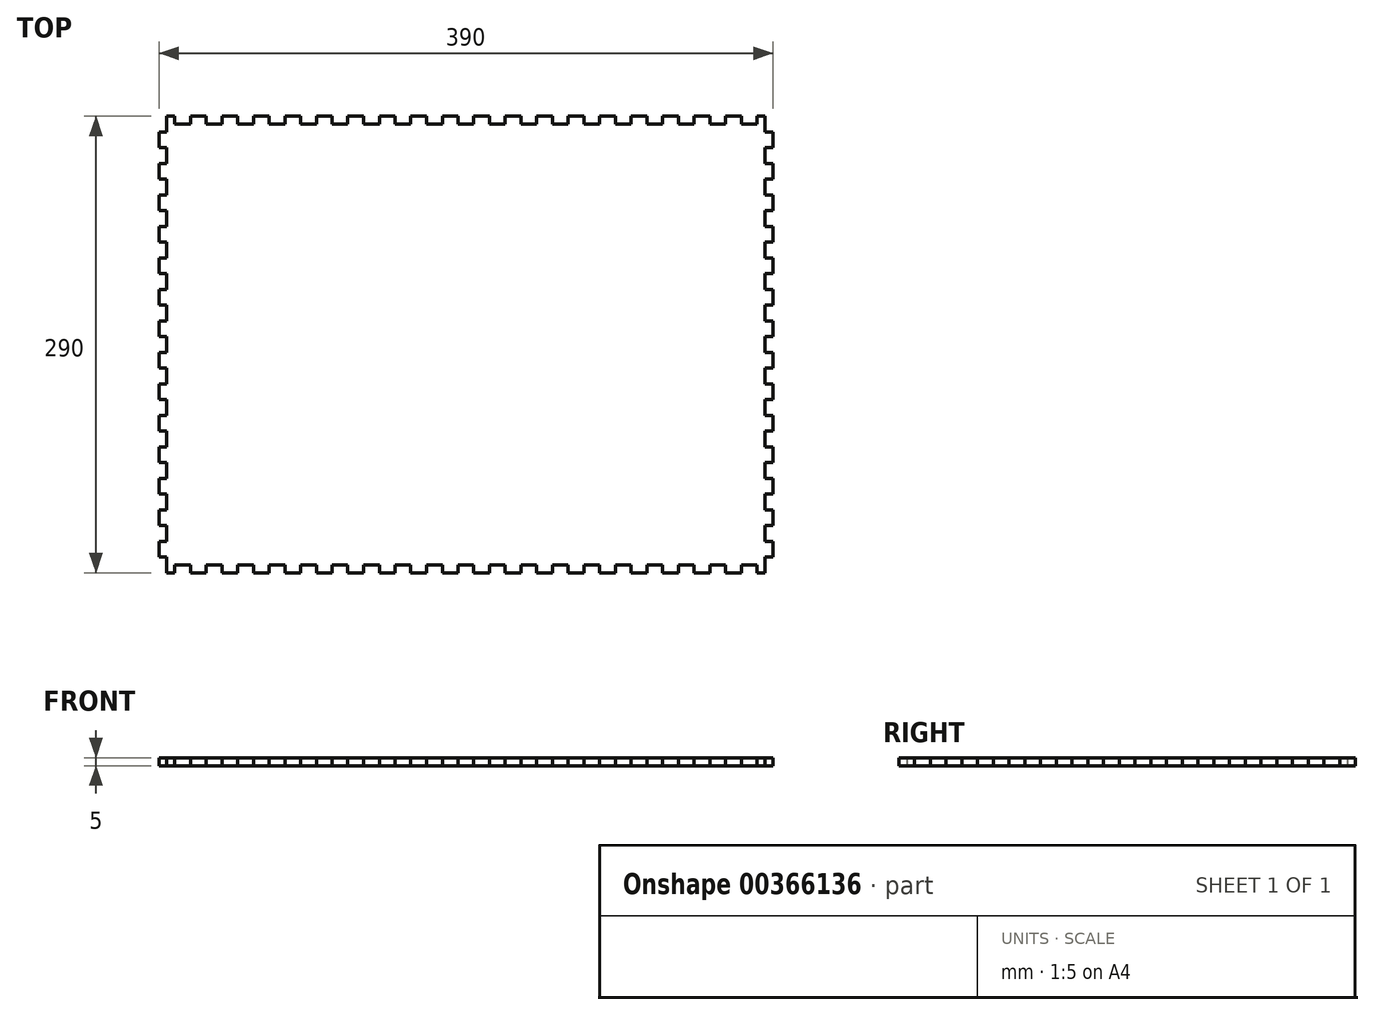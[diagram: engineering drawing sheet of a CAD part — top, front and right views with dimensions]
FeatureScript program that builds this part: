
annotation { "Feature Type Name" : "Feature", "Feature Type Description" : "" }
export const myFeature = defineFeature(function(context is Context, id is Id, definition is map)
    precondition{}
    {
        {
            var Q0;
            Q0=qCreatedBy(makeId("Top.planeOp"),FACE);
            var sketch = newSketch(context, id + "F0", { "sketchPlane" : qUnion([Q0])});
            skLineSegment(sketch, "E0", {"start": v(-189.05, -126.62) * mm, "end": v(-184.05, -126.62) * mm});
            skLineSegment(sketch, "E1", {"start": v(-184.05, -126.62) * mm, "end": v(-184.05, -136.62) * mm});
            skLineSegment(sketch, "E2", {"start": v(-184.05, -136.62) * mm, "end": v(-179.05, -136.62) * mm});
            skLineSegment(sketch, "E3", {"start": v(-179.05, -136.62) * mm, "end": v(-179.05, -131.62) * mm});
            skLineSegment(sketch, "E4", {"start": v(-179.05, -131.62) * mm, "end": v(-169.05, -131.62) * mm});
            skLineSegment(sketch, "E5", {"start": v(-169.05, -131.62) * mm, "end": v(-169.05, -136.62) * mm});
            skLineSegment(sketch, "E6", {"start": v(-169.05, -136.62) * mm, "end": v(-159.05, -136.62) * mm});
            skLineSegment(sketch, "E7", {"start": v(-159.05, -136.62) * mm, "end": v(-159.05, -131.62) * mm});
            skLineSegment(sketch, "E8", {"start": v(-159.05, -131.62) * mm, "end": v(-149.05, -131.62) * mm});
            skLineSegment(sketch, "E9", {"start": v(-149.05, -131.62) * mm, "end": v(-149.05, -136.62) * mm});
            skLineSegment(sketch, "E10.1.0.0", {"start": v(-149.05, -136.62) * mm, "end": v(-139.05, -136.62) * mm});
            skLineSegment(sketch, "E10.1.0.1", {"start": v(-139.05, -136.62) * mm, "end": v(-139.05, -131.62) * mm});
            skLineSegment(sketch, "E10.1.0.2", {"start": v(-139.05, -131.62) * mm, "end": v(-129.05, -131.62) * mm});
            skLineSegment(sketch, "E10.1.0.3", {"start": v(-129.05, -131.62) * mm, "end": v(-129.05, -136.62) * mm});
            skLineSegment(sketch, "E10.2.0.0", {"start": v(-129.05, -136.62) * mm, "end": v(-119.05, -136.62) * mm});
            skLineSegment(sketch, "E10.2.0.1", {"start": v(-119.05, -136.62) * mm, "end": v(-119.05, -131.62) * mm});
            skLineSegment(sketch, "E10.2.0.2", {"start": v(-119.05, -131.62) * mm, "end": v(-109.05, -131.62) * mm});
            skLineSegment(sketch, "E10.2.0.3", {"start": v(-109.05, -131.62) * mm, "end": v(-109.05, -136.62) * mm});
            skLineSegment(sketch, "E10.3.0.0", {"start": v(-109.05, -136.62) * mm, "end": v(-99.05, -136.62) * mm});
            skLineSegment(sketch, "E10.3.0.1", {"start": v(-99.05, -136.62) * mm, "end": v(-99.05, -131.62) * mm});
            skLineSegment(sketch, "E10.3.0.2", {"start": v(-99.05, -131.62) * mm, "end": v(-89.05, -131.62) * mm});
            skLineSegment(sketch, "E10.3.0.3", {"start": v(-89.05, -131.62) * mm, "end": v(-89.05, -136.62) * mm});
            skLineSegment(sketch, "E10.4.0.0", {"start": v(-89.05, -136.62) * mm, "end": v(-79.05, -136.62) * mm});
            skLineSegment(sketch, "E10.4.0.1", {"start": v(-79.05, -136.62) * mm, "end": v(-79.05, -131.62) * mm});
            skLineSegment(sketch, "E10.4.0.2", {"start": v(-79.05, -131.62) * mm, "end": v(-69.05, -131.62) * mm});
            skLineSegment(sketch, "E10.4.0.3", {"start": v(-69.05, -131.62) * mm, "end": v(-69.05, -136.62) * mm});
            skLineSegment(sketch, "E10.5.0.0", {"start": v(-69.05, -136.62) * mm, "end": v(-59.05, -136.62) * mm});
            skLineSegment(sketch, "E10.5.0.1", {"start": v(-59.05, -136.62) * mm, "end": v(-59.05, -131.62) * mm});
            skLineSegment(sketch, "E10.5.0.2", {"start": v(-59.05, -131.62) * mm, "end": v(-49.05, -131.62) * mm});
            skLineSegment(sketch, "E10.5.0.3", {"start": v(-49.05, -131.62) * mm, "end": v(-49.05, -136.62) * mm});
            skLineSegment(sketch, "E10.6.0.0", {"start": v(-49.05, -136.62) * mm, "end": v(-39.05, -136.62) * mm});
            skLineSegment(sketch, "E10.6.0.1", {"start": v(-39.05, -136.62) * mm, "end": v(-39.05, -131.62) * mm});
            skLineSegment(sketch, "E10.6.0.2", {"start": v(-39.05, -131.62) * mm, "end": v(-29.05, -131.62) * mm});
            skLineSegment(sketch, "E10.6.0.3", {"start": v(-29.05, -131.62) * mm, "end": v(-29.05, -136.62) * mm});
            skLineSegment(sketch, "E10.7.0.0", {"start": v(-29.05, -136.62) * mm, "end": v(-19.05, -136.62) * mm});
            skLineSegment(sketch, "E10.7.0.1", {"start": v(-19.05, -136.62) * mm, "end": v(-19.05, -131.62) * mm});
            skLineSegment(sketch, "E10.7.0.2", {"start": v(-19.05, -131.62) * mm, "end": v(-9.05, -131.62) * mm});
            skLineSegment(sketch, "E10.7.0.3", {"start": v(-9.05, -131.62) * mm, "end": v(-9.05, -136.62) * mm});
            skLineSegment(sketch, "E10.8.0.0", {"start": v(-9.05, -136.62) * mm, "end": v(0.95, -136.62) * mm});
            skLineSegment(sketch, "E10.8.0.1", {"start": v(0.95, -136.62) * mm, "end": v(0.95, -131.62) * mm});
            skLineSegment(sketch, "E10.8.0.2", {"start": v(0.95, -131.62) * mm, "end": v(10.95, -131.62) * mm});
            skLineSegment(sketch, "E10.8.0.3", {"start": v(10.95, -131.62) * mm, "end": v(10.95, -136.62) * mm});
            skLineSegment(sketch, "E10.9.0.0", {"start": v(10.95, -136.62) * mm, "end": v(20.95, -136.62) * mm});
            skLineSegment(sketch, "E10.9.0.1", {"start": v(20.95, -136.62) * mm, "end": v(20.95, -131.62) * mm});
            skLineSegment(sketch, "E10.9.0.2", {"start": v(20.95, -131.62) * mm, "end": v(30.95, -131.62) * mm});
            skLineSegment(sketch, "E10.9.0.3", {"start": v(30.95, -131.62) * mm, "end": v(30.95, -136.62) * mm});
            skLineSegment(sketch, "E10.10.0.0", {"start": v(30.95, -136.62) * mm, "end": v(40.95, -136.62) * mm});
            skLineSegment(sketch, "E10.10.0.1", {"start": v(40.95, -136.62) * mm, "end": v(40.95, -131.62) * mm});
            skLineSegment(sketch, "E10.10.0.2", {"start": v(40.95, -131.62) * mm, "end": v(50.95, -131.62) * mm});
            skLineSegment(sketch, "E10.10.0.3", {"start": v(50.95, -131.62) * mm, "end": v(50.95, -136.62) * mm});
            skLineSegment(sketch, "E10.11.0.0", {"start": v(50.95, -136.62) * mm, "end": v(60.95, -136.62) * mm});
            skLineSegment(sketch, "E10.11.0.1", {"start": v(60.95, -136.62) * mm, "end": v(60.95, -131.62) * mm});
            skLineSegment(sketch, "E10.11.0.2", {"start": v(60.95, -131.62) * mm, "end": v(70.95, -131.62) * mm});
            skLineSegment(sketch, "E10.11.0.3", {"start": v(70.95, -131.62) * mm, "end": v(70.95, -136.62) * mm});
            skLineSegment(sketch, "E10.12.0.0", {"start": v(70.95, -136.62) * mm, "end": v(80.95, -136.62) * mm});
            skLineSegment(sketch, "E10.12.0.1", {"start": v(80.95, -136.62) * mm, "end": v(80.95, -131.62) * mm});
            skLineSegment(sketch, "E10.12.0.2", {"start": v(80.95, -131.62) * mm, "end": v(90.95, -131.62) * mm});
            skLineSegment(sketch, "E10.12.0.3", {"start": v(90.95, -131.62) * mm, "end": v(90.95, -136.62) * mm});
            skLineSegment(sketch, "E10.13.0.0", {"start": v(90.95, -136.62) * mm, "end": v(100.95, -136.62) * mm});
            skLineSegment(sketch, "E10.13.0.1", {"start": v(100.95, -136.62) * mm, "end": v(100.95, -131.62) * mm});
            skLineSegment(sketch, "E10.13.0.2", {"start": v(100.95, -131.62) * mm, "end": v(110.95, -131.62) * mm});
            skLineSegment(sketch, "E10.13.0.3", {"start": v(110.95, -131.62) * mm, "end": v(110.95, -136.62) * mm});
            skLineSegment(sketch, "E10.14.0.0", {"start": v(110.95, -136.62) * mm, "end": v(120.95, -136.62) * mm});
            skLineSegment(sketch, "E10.14.0.1", {"start": v(120.95, -136.62) * mm, "end": v(120.95, -131.62) * mm});
            skLineSegment(sketch, "E10.14.0.2", {"start": v(120.95, -131.62) * mm, "end": v(130.95, -131.62) * mm});
            skLineSegment(sketch, "E10.14.0.3", {"start": v(130.95, -131.62) * mm, "end": v(130.95, -136.62) * mm});
            skLineSegment(sketch, "E10.15.0.0", {"start": v(130.95, -136.62) * mm, "end": v(140.95, -136.62) * mm});
            skLineSegment(sketch, "E10.15.0.1", {"start": v(140.95, -136.62) * mm, "end": v(140.95, -131.62) * mm});
            skLineSegment(sketch, "E10.15.0.2", {"start": v(140.95, -131.62) * mm, "end": v(150.95, -131.62) * mm});
            skLineSegment(sketch, "E10.15.0.3", {"start": v(150.95, -131.62) * mm, "end": v(150.95, -136.62) * mm});
            skLineSegment(sketch, "E10.16.0.0", {"start": v(150.95, -136.62) * mm, "end": v(160.95, -136.62) * mm});
            skLineSegment(sketch, "E10.16.0.1", {"start": v(160.95, -136.62) * mm, "end": v(160.95, -131.62) * mm});
            skLineSegment(sketch, "E10.16.0.2", {"start": v(160.95, -131.62) * mm, "end": v(170.95, -131.62) * mm});
            skLineSegment(sketch, "E10.16.0.3", {"start": v(170.95, -131.62) * mm, "end": v(170.95, -136.62) * mm});
            skLineSegment(sketch, "E10.17.0.0", {"start": v(170.95, -136.62) * mm, "end": v(180.95, -136.62) * mm});
            skLineSegment(sketch, "E10.17.0.1", {"start": v(180.95, -136.62) * mm, "end": v(180.95, -131.62) * mm});
            skLineSegment(sketch, "E10.17.0.2", {"start": v(180.95, -131.62) * mm, "end": v(190.95, -131.62) * mm});
            skLineSegment(sketch, "E10.17.0.3", {"start": v(190.95, -131.62) * mm, "end": v(190.95, -136.62) * mm});
            skLineSegment(sketch, "E10.direction1", {"start": v(-169.05, -136.62) * mm, "end": v(-149.05, -136.62) * mm, "construction": true});
            skLineSegment(sketch, "E11", {"start": v(190.95, -136.62) * mm, "end": v(195.95, -136.62) * mm});
            skLineSegment(sketch, "E12", {"start": v(195.95, -136.62) * mm, "end": v(195.95, -126.62) * mm});
            skLineSegment(sketch, "E13", {"start": v(195.95, -126.62) * mm, "end": v(200.95, -126.62) * mm});
            skLineSegment(sketch, "E14", {"start": v(200.95, 143.38) * mm, "end": v(195.95, 143.38) * mm});
            skLineSegment(sketch, "E15", {"start": v(195.95, 143.38) * mm, "end": v(195.95, 153.38) * mm});
            skLineSegment(sketch, "E16", {"start": v(195.95, 153.38) * mm, "end": v(190.95, 153.38) * mm});
            skLineSegment(sketch, "E17", {"start": v(190.95, 153.38) * mm, "end": v(190.95, 148.38) * mm});
            skLineSegment(sketch, "E18", {"start": v(190.95, 148.38) * mm, "end": v(180.95, 148.38) * mm});
            skLineSegment(sketch, "E19", {"start": v(180.95, 148.38) * mm, "end": v(180.95, 153.38) * mm});
            skLineSegment(sketch, "E20", {"start": v(180.95, 153.38) * mm, "end": v(170.95, 153.38) * mm});
            skLineSegment(sketch, "E21", {"start": v(170.95, 153.38) * mm, "end": v(170.95, 148.38) * mm});
            skLineSegment(sketch, "E22", {"start": v(170.95, 148.38) * mm, "end": v(160.95, 148.38) * mm});
            skLineSegment(sketch, "E23", {"start": v(160.95, 148.38) * mm, "end": v(160.95, 153.38) * mm});
            skLineSegment(sketch, "E24.1.0.0", {"start": v(160.95, 153.38) * mm, "end": v(150.95, 153.38) * mm});
            skLineSegment(sketch, "E24.1.0.1", {"start": v(150.95, 153.38) * mm, "end": v(150.95, 148.38) * mm});
            skLineSegment(sketch, "E24.1.0.2", {"start": v(150.95, 148.38) * mm, "end": v(140.95, 148.38) * mm});
            skLineSegment(sketch, "E24.1.0.3", {"start": v(140.95, 148.38) * mm, "end": v(140.95, 153.38) * mm});
            skLineSegment(sketch, "E24.2.0.0", {"start": v(140.95, 153.38) * mm, "end": v(130.95, 153.38) * mm});
            skLineSegment(sketch, "E24.2.0.1", {"start": v(130.95, 153.38) * mm, "end": v(130.95, 148.38) * mm});
            skLineSegment(sketch, "E24.2.0.2", {"start": v(130.95, 148.38) * mm, "end": v(120.95, 148.38) * mm});
            skLineSegment(sketch, "E24.2.0.3", {"start": v(120.95, 148.38) * mm, "end": v(120.95, 153.38) * mm});
            skLineSegment(sketch, "E24.3.0.0", {"start": v(120.95, 153.38) * mm, "end": v(110.95, 153.38) * mm});
            skLineSegment(sketch, "E24.3.0.1", {"start": v(110.95, 153.38) * mm, "end": v(110.95, 148.38) * mm});
            skLineSegment(sketch, "E24.3.0.2", {"start": v(110.95, 148.38) * mm, "end": v(100.95, 148.38) * mm});
            skLineSegment(sketch, "E24.3.0.3", {"start": v(100.95, 148.38) * mm, "end": v(100.95, 153.38) * mm});
            skLineSegment(sketch, "E24.4.0.0", {"start": v(100.95, 153.38) * mm, "end": v(90.95, 153.38) * mm});
            skLineSegment(sketch, "E24.4.0.1", {"start": v(90.95, 153.38) * mm, "end": v(90.95, 148.38) * mm});
            skLineSegment(sketch, "E24.4.0.2", {"start": v(90.95, 148.38) * mm, "end": v(80.95, 148.38) * mm});
            skLineSegment(sketch, "E24.4.0.3", {"start": v(80.95, 148.38) * mm, "end": v(80.95, 153.38) * mm});
            skLineSegment(sketch, "E24.5.0.0", {"start": v(80.95, 153.38) * mm, "end": v(70.95, 153.38) * mm});
            skLineSegment(sketch, "E24.5.0.1", {"start": v(70.95, 153.38) * mm, "end": v(70.95, 148.38) * mm});
            skLineSegment(sketch, "E24.5.0.2", {"start": v(70.95, 148.38) * mm, "end": v(60.95, 148.38) * mm});
            skLineSegment(sketch, "E24.5.0.3", {"start": v(60.95, 148.38) * mm, "end": v(60.95, 153.38) * mm});
            skLineSegment(sketch, "E24.6.0.0", {"start": v(60.95, 153.38) * mm, "end": v(50.95, 153.38) * mm});
            skLineSegment(sketch, "E24.6.0.1", {"start": v(50.95, 153.38) * mm, "end": v(50.95, 148.38) * mm});
            skLineSegment(sketch, "E24.6.0.2", {"start": v(50.95, 148.38) * mm, "end": v(40.95, 148.38) * mm});
            skLineSegment(sketch, "E24.6.0.3", {"start": v(40.95, 148.38) * mm, "end": v(40.95, 153.38) * mm});
            skLineSegment(sketch, "E24.7.0.0", {"start": v(40.95, 153.38) * mm, "end": v(30.95, 153.38) * mm});
            skLineSegment(sketch, "E24.7.0.1", {"start": v(30.95, 153.38) * mm, "end": v(30.95, 148.38) * mm});
            skLineSegment(sketch, "E24.7.0.2", {"start": v(30.95, 148.38) * mm, "end": v(20.95, 148.38) * mm});
            skLineSegment(sketch, "E24.7.0.3", {"start": v(20.95, 148.38) * mm, "end": v(20.95, 153.38) * mm});
            skLineSegment(sketch, "E24.8.0.0", {"start": v(20.95, 153.38) * mm, "end": v(10.95, 153.38) * mm});
            skLineSegment(sketch, "E24.8.0.1", {"start": v(10.95, 153.38) * mm, "end": v(10.95, 148.38) * mm});
            skLineSegment(sketch, "E24.8.0.2", {"start": v(10.95, 148.38) * mm, "end": v(0.95, 148.38) * mm});
            skLineSegment(sketch, "E24.8.0.3", {"start": v(0.95, 148.38) * mm, "end": v(0.95, 153.38) * mm});
            skLineSegment(sketch, "E24.9.0.0", {"start": v(0.95, 153.38) * mm, "end": v(-9.05, 153.38) * mm});
            skLineSegment(sketch, "E24.9.0.1", {"start": v(-9.05, 153.38) * mm, "end": v(-9.05, 148.38) * mm});
            skLineSegment(sketch, "E24.9.0.2", {"start": v(-9.05, 148.38) * mm, "end": v(-19.05, 148.38) * mm});
            skLineSegment(sketch, "E24.9.0.3", {"start": v(-19.05, 148.38) * mm, "end": v(-19.05, 153.38) * mm});
            skLineSegment(sketch, "E24.10.0.0", {"start": v(-19.05, 153.38) * mm, "end": v(-29.05, 153.38) * mm});
            skLineSegment(sketch, "E24.10.0.1", {"start": v(-29.05, 153.38) * mm, "end": v(-29.05, 148.38) * mm});
            skLineSegment(sketch, "E24.10.0.2", {"start": v(-29.05, 148.38) * mm, "end": v(-39.05, 148.38) * mm});
            skLineSegment(sketch, "E24.10.0.3", {"start": v(-39.05, 148.38) * mm, "end": v(-39.05, 153.38) * mm});
            skLineSegment(sketch, "E24.11.0.0", {"start": v(-39.05, 153.38) * mm, "end": v(-49.05, 153.38) * mm});
            skLineSegment(sketch, "E24.11.0.1", {"start": v(-49.05, 153.38) * mm, "end": v(-49.05, 148.38) * mm});
            skLineSegment(sketch, "E24.11.0.2", {"start": v(-49.05, 148.38) * mm, "end": v(-59.05, 148.38) * mm});
            skLineSegment(sketch, "E24.11.0.3", {"start": v(-59.05, 148.38) * mm, "end": v(-59.05, 153.38) * mm});
            skLineSegment(sketch, "E24.12.0.0", {"start": v(-59.05, 153.38) * mm, "end": v(-69.05, 153.38) * mm});
            skLineSegment(sketch, "E24.12.0.1", {"start": v(-69.05, 153.38) * mm, "end": v(-69.05, 148.38) * mm});
            skLineSegment(sketch, "E24.12.0.2", {"start": v(-69.05, 148.38) * mm, "end": v(-79.05, 148.38) * mm});
            skLineSegment(sketch, "E24.12.0.3", {"start": v(-79.05, 148.38) * mm, "end": v(-79.05, 153.38) * mm});
            skLineSegment(sketch, "E24.13.0.0", {"start": v(-79.05, 153.38) * mm, "end": v(-89.05, 153.38) * mm});
            skLineSegment(sketch, "E24.13.0.1", {"start": v(-89.05, 153.38) * mm, "end": v(-89.05, 148.38) * mm});
            skLineSegment(sketch, "E24.13.0.2", {"start": v(-89.05, 148.38) * mm, "end": v(-99.05, 148.38) * mm});
            skLineSegment(sketch, "E24.13.0.3", {"start": v(-99.05, 148.38) * mm, "end": v(-99.05, 153.38) * mm});
            skLineSegment(sketch, "E24.14.0.0", {"start": v(-99.05, 153.38) * mm, "end": v(-109.05, 153.38) * mm});
            skLineSegment(sketch, "E24.14.0.1", {"start": v(-109.05, 153.38) * mm, "end": v(-109.05, 148.38) * mm});
            skLineSegment(sketch, "E24.14.0.2", {"start": v(-109.05, 148.38) * mm, "end": v(-119.05, 148.38) * mm});
            skLineSegment(sketch, "E24.14.0.3", {"start": v(-119.05, 148.38) * mm, "end": v(-119.05, 153.38) * mm});
            skLineSegment(sketch, "E24.15.0.0", {"start": v(-119.05, 153.38) * mm, "end": v(-129.05, 153.38) * mm});
            skLineSegment(sketch, "E24.15.0.1", {"start": v(-129.05, 153.38) * mm, "end": v(-129.05, 148.38) * mm});
            skLineSegment(sketch, "E24.15.0.2", {"start": v(-129.05, 148.38) * mm, "end": v(-139.05, 148.38) * mm});
            skLineSegment(sketch, "E24.15.0.3", {"start": v(-139.05, 148.38) * mm, "end": v(-139.05, 153.38) * mm});
            skLineSegment(sketch, "E24.16.0.0", {"start": v(-139.05, 153.38) * mm, "end": v(-149.05, 153.38) * mm});
            skLineSegment(sketch, "E24.16.0.1", {"start": v(-149.05, 153.38) * mm, "end": v(-149.05, 148.38) * mm});
            skLineSegment(sketch, "E24.16.0.2", {"start": v(-149.05, 148.38) * mm, "end": v(-159.05, 148.38) * mm});
            skLineSegment(sketch, "E24.16.0.3", {"start": v(-159.05, 148.38) * mm, "end": v(-159.05, 153.38) * mm});
            skLineSegment(sketch, "E24.17.0.0", {"start": v(-159.05, 153.38) * mm, "end": v(-169.05, 153.38) * mm});
            skLineSegment(sketch, "E24.17.0.1", {"start": v(-169.05, 153.38) * mm, "end": v(-169.05, 148.38) * mm});
            skLineSegment(sketch, "E24.17.0.2", {"start": v(-169.05, 148.38) * mm, "end": v(-179.05, 148.38) * mm});
            skLineSegment(sketch, "E24.17.0.3", {"start": v(-179.05, 148.38) * mm, "end": v(-179.05, 153.38) * mm});
            skLineSegment(sketch, "E24.direction1", {"start": v(180.95, 153.38) * mm, "end": v(160.95, 153.38) * mm, "construction": true});
            skLineSegment(sketch, "E25", {"start": v(-179.05, 153.38) * mm, "end": v(-184.05, 153.38) * mm});
            skLineSegment(sketch, "E26", {"start": v(-184.05, 153.38) * mm, "end": v(-184.05, 143.38) * mm});
            skLineSegment(sketch, "E27", {"start": v(-184.05, 143.38) * mm, "end": v(-189.05, 143.38) * mm});
            skLineSegment(sketch, "E28", {"start": v(-189.05, 143.38) * mm, "end": v(-189.05, 133.38) * mm});
            skLineSegment(sketch, "E29", {"start": v(-189.05, 133.38) * mm, "end": v(-184.05, 133.38) * mm});
            skLineSegment(sketch, "E30", {"start": v(-184.05, 133.38) * mm, "end": v(-184.05, 123.38) * mm});
            skLineSegment(sketch, "E31.1.0.0", {"start": v(-184.05, 123.38) * mm, "end": v(-189.05, 123.38) * mm});
            skLineSegment(sketch, "E31.1.0.1", {"start": v(-189.05, 123.38) * mm, "end": v(-189.05, 113.38) * mm});
            skLineSegment(sketch, "E31.1.0.2", {"start": v(-189.05, 113.38) * mm, "end": v(-184.05, 113.38) * mm});
            skLineSegment(sketch, "E31.1.0.3", {"start": v(-184.05, 113.38) * mm, "end": v(-184.05, 103.38) * mm});
            skLineSegment(sketch, "E31.2.0.0", {"start": v(-184.05, 103.38) * mm, "end": v(-189.05, 103.38) * mm});
            skLineSegment(sketch, "E31.2.0.1", {"start": v(-189.05, 103.38) * mm, "end": v(-189.05, 93.38) * mm});
            skLineSegment(sketch, "E31.2.0.2", {"start": v(-189.05, 93.38) * mm, "end": v(-184.05, 93.38) * mm});
            skLineSegment(sketch, "E31.2.0.3", {"start": v(-184.05, 93.38) * mm, "end": v(-184.05, 83.38) * mm});
            skLineSegment(sketch, "E31.3.0.0", {"start": v(-184.05, 83.38) * mm, "end": v(-189.05, 83.38) * mm});
            skLineSegment(sketch, "E31.3.0.1", {"start": v(-189.05, 83.38) * mm, "end": v(-189.05, 73.38) * mm});
            skLineSegment(sketch, "E31.3.0.2", {"start": v(-189.05, 73.38) * mm, "end": v(-184.05, 73.38) * mm});
            skLineSegment(sketch, "E31.3.0.3", {"start": v(-184.05, 73.38) * mm, "end": v(-184.05, 63.38) * mm});
            skLineSegment(sketch, "E31.4.0.0", {"start": v(-184.05, 63.38) * mm, "end": v(-189.05, 63.38) * mm});
            skLineSegment(sketch, "E31.4.0.1", {"start": v(-189.05, 63.38) * mm, "end": v(-189.05, 53.38) * mm});
            skLineSegment(sketch, "E31.4.0.2", {"start": v(-189.05, 53.38) * mm, "end": v(-184.05, 53.38) * mm});
            skLineSegment(sketch, "E31.4.0.3", {"start": v(-184.05, 53.38) * mm, "end": v(-184.05, 43.38) * mm});
            skLineSegment(sketch, "E31.5.0.0", {"start": v(-184.05, 43.38) * mm, "end": v(-189.05, 43.38) * mm});
            skLineSegment(sketch, "E31.5.0.1", {"start": v(-189.05, 43.38) * mm, "end": v(-189.05, 33.38) * mm});
            skLineSegment(sketch, "E31.5.0.2", {"start": v(-189.05, 33.38) * mm, "end": v(-184.05, 33.38) * mm});
            skLineSegment(sketch, "E31.5.0.3", {"start": v(-184.05, 33.38) * mm, "end": v(-184.05, 23.38) * mm});
            skLineSegment(sketch, "E31.6.0.0", {"start": v(-184.05, 23.38) * mm, "end": v(-189.05, 23.38) * mm});
            skLineSegment(sketch, "E31.6.0.1", {"start": v(-189.05, 23.38) * mm, "end": v(-189.05, 13.38) * mm});
            skLineSegment(sketch, "E31.6.0.2", {"start": v(-189.05, 13.38) * mm, "end": v(-184.05, 13.38) * mm});
            skLineSegment(sketch, "E31.6.0.3", {"start": v(-184.05, 13.38) * mm, "end": v(-184.05, 3.38) * mm});
            skLineSegment(sketch, "E31.7.0.0", {"start": v(-184.05, 3.38) * mm, "end": v(-189.05, 3.38) * mm});
            skLineSegment(sketch, "E31.7.0.1", {"start": v(-189.05, 3.38) * mm, "end": v(-189.05, -6.62) * mm});
            skLineSegment(sketch, "E31.7.0.2", {"start": v(-189.05, -6.62) * mm, "end": v(-184.05, -6.62) * mm});
            skLineSegment(sketch, "E31.7.0.3", {"start": v(-184.05, -6.62) * mm, "end": v(-184.05, -16.62) * mm});
            skLineSegment(sketch, "E31.8.0.0", {"start": v(-184.05, -16.62) * mm, "end": v(-189.05, -16.62) * mm});
            skLineSegment(sketch, "E31.8.0.1", {"start": v(-189.05, -16.62) * mm, "end": v(-189.05, -26.62) * mm});
            skLineSegment(sketch, "E31.8.0.2", {"start": v(-189.05, -26.62) * mm, "end": v(-184.05, -26.62) * mm});
            skLineSegment(sketch, "E31.8.0.3", {"start": v(-184.05, -26.62) * mm, "end": v(-184.05, -36.62) * mm});
            skLineSegment(sketch, "E31.9.0.0", {"start": v(-184.05, -36.62) * mm, "end": v(-189.05, -36.62) * mm});
            skLineSegment(sketch, "E31.9.0.1", {"start": v(-189.05, -36.62) * mm, "end": v(-189.05, -46.62) * mm});
            skLineSegment(sketch, "E31.9.0.2", {"start": v(-189.05, -46.62) * mm, "end": v(-184.05, -46.62) * mm});
            skLineSegment(sketch, "E31.9.0.3", {"start": v(-184.05, -46.62) * mm, "end": v(-184.05, -56.62) * mm});
            skLineSegment(sketch, "E31.10.0.0", {"start": v(-184.05, -56.62) * mm, "end": v(-189.05, -56.62) * mm});
            skLineSegment(sketch, "E31.10.0.1", {"start": v(-189.05, -56.62) * mm, "end": v(-189.05, -66.62) * mm});
            skLineSegment(sketch, "E31.10.0.2", {"start": v(-189.05, -66.62) * mm, "end": v(-184.05, -66.62) * mm});
            skLineSegment(sketch, "E31.10.0.3", {"start": v(-184.05, -66.62) * mm, "end": v(-184.05, -76.62) * mm});
            skLineSegment(sketch, "E31.11.0.0", {"start": v(-184.05, -76.62) * mm, "end": v(-189.05, -76.62) * mm});
            skLineSegment(sketch, "E31.11.0.1", {"start": v(-189.05, -76.62) * mm, "end": v(-189.05, -86.62) * mm});
            skLineSegment(sketch, "E31.11.0.2", {"start": v(-189.05, -86.62) * mm, "end": v(-184.05, -86.62) * mm});
            skLineSegment(sketch, "E31.11.0.3", {"start": v(-184.05, -86.62) * mm, "end": v(-184.05, -96.62) * mm});
            skLineSegment(sketch, "E31.12.0.0", {"start": v(-184.05, -96.62) * mm, "end": v(-189.05, -96.62) * mm});
            skLineSegment(sketch, "E31.12.0.1", {"start": v(-189.05, -96.62) * mm, "end": v(-189.05, -106.62) * mm});
            skLineSegment(sketch, "E31.12.0.2", {"start": v(-189.05, -106.62) * mm, "end": v(-184.05, -106.62) * mm});
            skLineSegment(sketch, "E31.12.0.3", {"start": v(-184.05, -106.62) * mm, "end": v(-184.05, -116.62) * mm});
            skLineSegment(sketch, "E31.13.0.0", {"start": v(-184.05, -116.62) * mm, "end": v(-189.05, -116.62) * mm});
            skLineSegment(sketch, "E31.13.0.1", {"start": v(-189.05, -116.62) * mm, "end": v(-189.05, -126.62) * mm});
            skLineSegment(sketch, "E32", {"start": v(200.95, -126.62) * mm, "end": v(200.95, -116.62) * mm});
            skLineSegment(sketch, "E33", {"start": v(200.95, -116.62) * mm, "end": v(195.95, -116.62) * mm});
            skLineSegment(sketch, "E34", {"start": v(195.95, -116.62) * mm, "end": v(195.95, -106.62) * mm});
            skLineSegment(sketch, "E35.1.0.0", {"start": v(195.95, -106.62) * mm, "end": v(200.95, -106.62) * mm});
            skLineSegment(sketch, "E35.1.0.1", {"start": v(200.95, -106.62) * mm, "end": v(200.95, -96.62) * mm});
            skLineSegment(sketch, "E35.1.0.2", {"start": v(200.95, -96.62) * mm, "end": v(195.95, -96.62) * mm});
            skLineSegment(sketch, "E35.1.0.3", {"start": v(195.95, -96.62) * mm, "end": v(195.95, -86.62) * mm});
            skLineSegment(sketch, "E35.2.0.0", {"start": v(195.95, -86.62) * mm, "end": v(200.95, -86.62) * mm});
            skLineSegment(sketch, "E35.2.0.1", {"start": v(200.95, -86.62) * mm, "end": v(200.95, -76.62) * mm});
            skLineSegment(sketch, "E35.2.0.2", {"start": v(200.95, -76.62) * mm, "end": v(195.95, -76.62) * mm});
            skLineSegment(sketch, "E35.2.0.3", {"start": v(195.95, -76.62) * mm, "end": v(195.95, -66.62) * mm});
            skLineSegment(sketch, "E35.3.0.0", {"start": v(195.95, -66.62) * mm, "end": v(200.95, -66.62) * mm});
            skLineSegment(sketch, "E35.3.0.1", {"start": v(200.95, -66.62) * mm, "end": v(200.95, -56.62) * mm});
            skLineSegment(sketch, "E35.3.0.2", {"start": v(200.95, -56.62) * mm, "end": v(195.95, -56.62) * mm});
            skLineSegment(sketch, "E35.3.0.3", {"start": v(195.95, -56.62) * mm, "end": v(195.95, -46.62) * mm});
            skLineSegment(sketch, "E35.4.0.0", {"start": v(195.95, -46.62) * mm, "end": v(200.95, -46.62) * mm});
            skLineSegment(sketch, "E35.4.0.1", {"start": v(200.95, -46.62) * mm, "end": v(200.95, -36.62) * mm});
            skLineSegment(sketch, "E35.4.0.2", {"start": v(200.95, -36.62) * mm, "end": v(195.95, -36.62) * mm});
            skLineSegment(sketch, "E35.4.0.3", {"start": v(195.95, -36.62) * mm, "end": v(195.95, -26.62) * mm});
            skLineSegment(sketch, "E35.5.0.0", {"start": v(195.95, -26.62) * mm, "end": v(200.95, -26.62) * mm});
            skLineSegment(sketch, "E35.5.0.1", {"start": v(200.95, -26.62) * mm, "end": v(200.95, -16.62) * mm});
            skLineSegment(sketch, "E35.5.0.2", {"start": v(200.95, -16.62) * mm, "end": v(195.95, -16.62) * mm});
            skLineSegment(sketch, "E35.5.0.3", {"start": v(195.95, -16.62) * mm, "end": v(195.95, -6.62) * mm});
            skLineSegment(sketch, "E35.6.0.0", {"start": v(195.95, -6.62) * mm, "end": v(200.95, -6.62) * mm});
            skLineSegment(sketch, "E35.6.0.1", {"start": v(200.95, -6.62) * mm, "end": v(200.95, 3.38) * mm});
            skLineSegment(sketch, "E35.6.0.2", {"start": v(200.95, 3.38) * mm, "end": v(195.95, 3.38) * mm});
            skLineSegment(sketch, "E35.6.0.3", {"start": v(195.95, 3.38) * mm, "end": v(195.95, 13.38) * mm});
            skLineSegment(sketch, "E35.7.0.0", {"start": v(195.95, 13.38) * mm, "end": v(200.95, 13.38) * mm});
            skLineSegment(sketch, "E35.7.0.1", {"start": v(200.95, 13.38) * mm, "end": v(200.95, 23.38) * mm});
            skLineSegment(sketch, "E35.7.0.2", {"start": v(200.95, 23.38) * mm, "end": v(195.95, 23.38) * mm});
            skLineSegment(sketch, "E35.7.0.3", {"start": v(195.95, 23.38) * mm, "end": v(195.95, 33.38) * mm});
            skLineSegment(sketch, "E35.8.0.0", {"start": v(195.95, 33.38) * mm, "end": v(200.95, 33.38) * mm});
            skLineSegment(sketch, "E35.8.0.1", {"start": v(200.95, 33.38) * mm, "end": v(200.95, 43.38) * mm});
            skLineSegment(sketch, "E35.8.0.2", {"start": v(200.95, 43.38) * mm, "end": v(195.95, 43.38) * mm});
            skLineSegment(sketch, "E35.8.0.3", {"start": v(195.95, 43.38) * mm, "end": v(195.95, 53.38) * mm});
            skLineSegment(sketch, "E35.9.0.0", {"start": v(195.95, 53.38) * mm, "end": v(200.95, 53.38) * mm});
            skLineSegment(sketch, "E35.9.0.1", {"start": v(200.95, 53.38) * mm, "end": v(200.95, 63.38) * mm});
            skLineSegment(sketch, "E35.9.0.2", {"start": v(200.95, 63.38) * mm, "end": v(195.95, 63.38) * mm});
            skLineSegment(sketch, "E35.9.0.3", {"start": v(195.95, 63.38) * mm, "end": v(195.95, 73.38) * mm});
            skLineSegment(sketch, "E35.10.0.0", {"start": v(195.95, 73.38) * mm, "end": v(200.95, 73.38) * mm});
            skLineSegment(sketch, "E35.10.0.1", {"start": v(200.95, 73.38) * mm, "end": v(200.95, 83.38) * mm});
            skLineSegment(sketch, "E35.10.0.2", {"start": v(200.95, 83.38) * mm, "end": v(195.95, 83.38) * mm});
            skLineSegment(sketch, "E35.10.0.3", {"start": v(195.95, 83.38) * mm, "end": v(195.95, 93.38) * mm});
            skLineSegment(sketch, "E35.11.0.0", {"start": v(195.95, 93.38) * mm, "end": v(200.95, 93.38) * mm});
            skLineSegment(sketch, "E35.11.0.1", {"start": v(200.95, 93.38) * mm, "end": v(200.95, 103.38) * mm});
            skLineSegment(sketch, "E35.11.0.2", {"start": v(200.95, 103.38) * mm, "end": v(195.95, 103.38) * mm});
            skLineSegment(sketch, "E35.11.0.3", {"start": v(195.95, 103.38) * mm, "end": v(195.95, 113.38) * mm});
            skLineSegment(sketch, "E35.12.0.0", {"start": v(195.95, 113.38) * mm, "end": v(200.95, 113.38) * mm});
            skLineSegment(sketch, "E35.12.0.1", {"start": v(200.95, 113.38) * mm, "end": v(200.95, 123.38) * mm});
            skLineSegment(sketch, "E35.12.0.2", {"start": v(200.95, 123.38) * mm, "end": v(195.95, 123.38) * mm});
            skLineSegment(sketch, "E35.12.0.3", {"start": v(195.95, 123.38) * mm, "end": v(195.95, 133.38) * mm});
            skLineSegment(sketch, "E35.13.0.0", {"start": v(195.95, 133.38) * mm, "end": v(200.95, 133.38) * mm});
            skLineSegment(sketch, "E35.13.0.1", {"start": v(200.95, 133.38) * mm, "end": v(200.95, 143.38) * mm});
            skSolve(sketch);
        }
        {
            var Q0;
            Q0 = qSketchRegion(id + "F0", true);
            extrude(context, id + "F1", {"entities" : qUnion([Q0]), "endBound" : BoundingType.SYMMETRIC, "depth" : 5 * mm});
        }
    });
